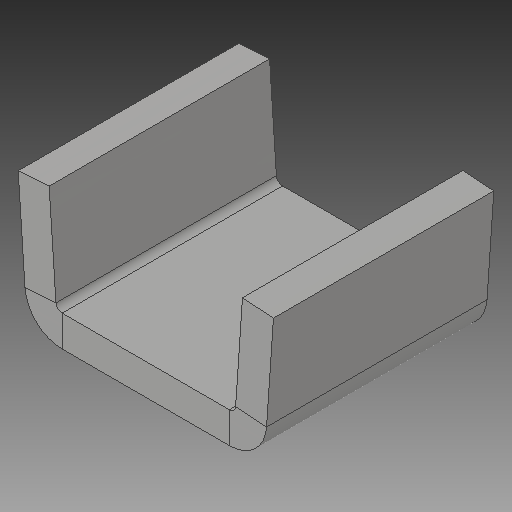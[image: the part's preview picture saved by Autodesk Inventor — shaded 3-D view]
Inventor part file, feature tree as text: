
AUTODESK INVENTOR PART (.ipt)
format: ipt  version: 2018 (Build 220112000, 112)  size: 123,904 bytes
history: native  units: mm
features: sheet_metal_op x4, sketch x2, other x2
ambient origin geometry x8: Origin, YZ Plane, XZ Plane, XY Plane, X Axis, Y Axis, Z Axis, Center Point
bodies: Solid1 (feature_tree)
feature tree (8):
  sheet_metal_op  "Face1"
  sheet_metal_op  "Flange1"
  sketch  "Sketch1"  dims[d0=35.5mm]
  other  "Plate1"
  sketch  "Sketch2"  dims[d1=5.0mm d2=5.0mm d3=2.5mm d4=10.0mm d5=1.0mm d6=21.37mm d7=15.009832mm d8=1.0mm d9=20.0mm d10=5.0mm d11=1.0mm d12=38.128mm]
  other  "Plate2"
  sheet_metal_op  "Bend1"
  sheet_metal_op  "Corner1"
